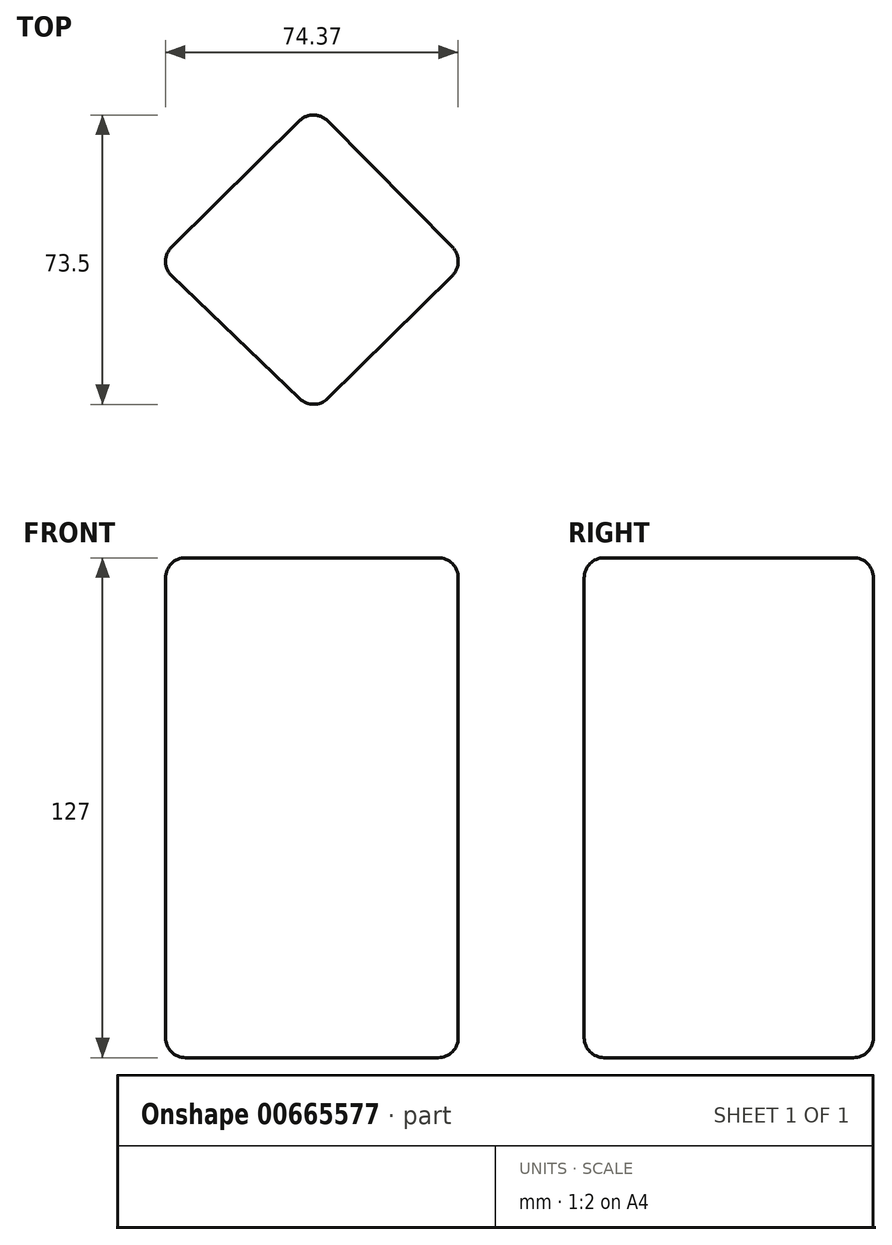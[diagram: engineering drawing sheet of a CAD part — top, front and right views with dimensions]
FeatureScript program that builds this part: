
annotation { "Feature Type Name" : "Feature", "Feature Type Description" : "" }
export const myFeature = defineFeature(function(context is Context, id is Id, definition is map)
    precondition{}
    {
        {
            var Q0;
            Q0=qCreatedBy(makeId("Top.planeOp"),FACE);
            var sketch = newSketch(context, id + "F0", { "sketchPlane" : qUnion([Q0])});
            skLineSegment(sketch, "E0", {"start": v(-39.88, 0) * mm, "end": v(0, 39.34) * mm});
            skLineSegment(sketch, "E1", {"start": v(0, 39.34) * mm, "end": v(38.8, 0) * mm});
            skLineSegment(sketch, "E2", {"start": v(38.8, 0) * mm, "end": v(0, -38.28) * mm});
            skLineSegment(sketch, "E3", {"start": v(0, -38.28) * mm, "end": v(-39.88, 0) * mm});
            skSolve(sketch);
        }
        {
            var Q0;
            Q0 = qSketchRegion(id + "F0", true);
            extrude(context, id + "F1", {"entities" : qUnion([Q0]), "endBound" : BoundingType.SYMMETRIC, "depth" : 127 * mm, "offsetDistance" : 25.4 * mm});
        }
        {
            var Q0;
            Q0=makeQuery(id+"F1.opExtrude","CAP_FACE",FACE,{"disambiguationData":[OSD([sQuery(id+"F0.wireOp",EDGE,"E0"),sQuery(id+"F0.wireOp",EDGE,"E1"),sQuery(id+"F0.wireOp",EDGE,"E2"),sQuery(id+"F0.wireOp",EDGE,"E3")])],"isStart":false});
            var sketch = newSketch(context, id + "F2", { "sketchPlane" : qUnion([Q0])});
            skSolve(sketch);
        }
        {
            var Q0;
            Q0=makeQuery(id+"F1.opExtrude","CAP_EDGE",EDGE,{"disambiguationData":[OSD([sQuery(id+"F0.wireOp",EDGE,"E1")])],"isStart":false});
            var Q1;
            Q1=makeQuery(id+"F1.opExtrude","SWEPT_FACE",FACE,{"disambiguationData":[OSD([sQuery(id+"F0.wireOp",EDGE,"E1")])]});
            var Q2;
            Q2=makeQuery(id+"F1.opExtrude","CAP_EDGE",EDGE,{"disambiguationData":[OSD([sQuery(id+"F0.wireOp",EDGE,"E2")])],"isStart":false});
            var Q3;
            Q3=makeQuery(id+"F1.opExtrude","CAP_EDGE",EDGE,{"disambiguationData":[OSD([sQuery(id+"F0.wireOp",EDGE,"E3")])],"isStart":false});
            var Q4;
            Q4=makeQuery(id+"F1.opExtrude","CAP_EDGE",EDGE,{"disambiguationData":[OSD([sQuery(id+"F0.wireOp",EDGE,"E0")])],"isStart":false});
            var Q5;
            Q5=makeQuery(id+"F1.opExtrude","SWEPT_EDGE",EDGE,{"disambiguationData":[OSD([sQuery(id+"F0.wireOp",EDGE,"E2"),sQuery(id+"F0.wireOp",EDGE,"E3")])]});
            var Q6;
            Q6=makeQuery(id+"F1.opExtrude","SWEPT_EDGE",EDGE,{"disambiguationData":[OSD([sQuery(id+"F0.wireOp",EDGE,"E0"),sQuery(id+"F0.wireOp",EDGE,"E3")])]});
            var Q7;
            Q7=makeQuery(id+"F1.opExtrude","CAP_EDGE",EDGE,{"disambiguationData":[OSD([sQuery(id+"F0.wireOp",EDGE,"E3")])],"isStart":true});
            var Q8;
            Q8=makeQuery(id+"F1.opExtrude","CAP_EDGE",EDGE,{"disambiguationData":[OSD([sQuery(id+"F0.wireOp",EDGE,"E2")])],"isStart":true});
            var Q9;
            Q9=makeQuery(id+"F1.opExtrude","CAP_EDGE",EDGE,{"disambiguationData":[OSD([sQuery(id+"F0.wireOp",EDGE,"E0")])],"isStart":true});
            fillet(context, id + "F3", {"entities" : qUnion([Q0, Q1, Q2, Q3, Q4, Q5, Q6, Q7, Q8, Q9]), "radius" : 5.08 * mm, "tangentPropagation" : true, "allowEdgeOverflow" : false});
        }
    });
